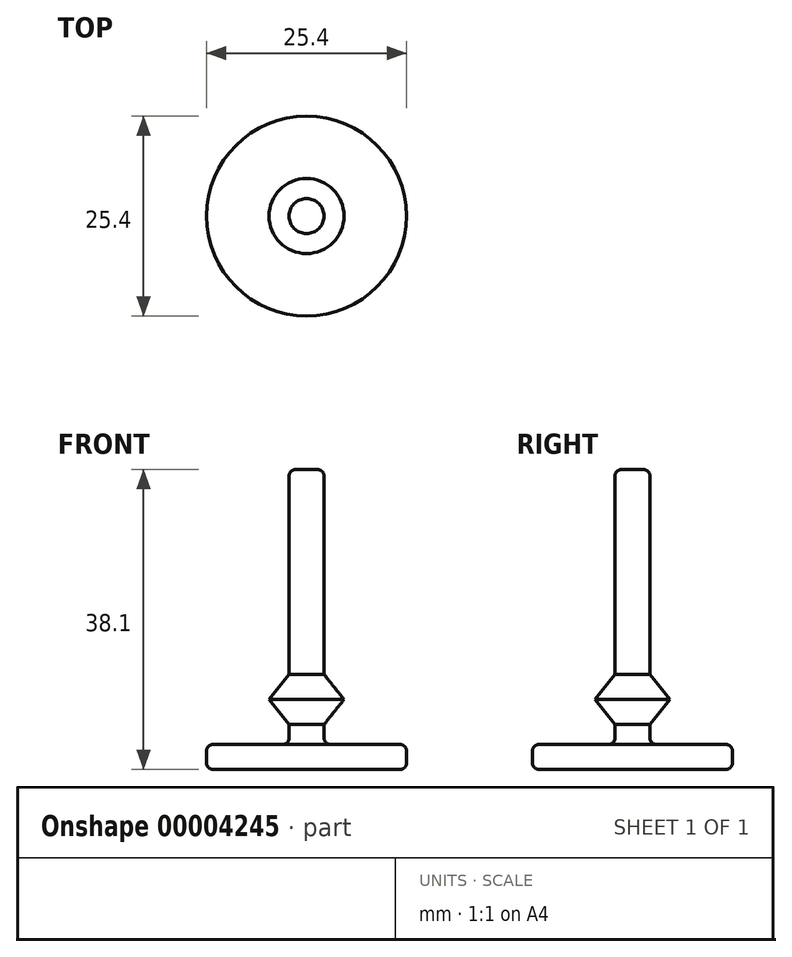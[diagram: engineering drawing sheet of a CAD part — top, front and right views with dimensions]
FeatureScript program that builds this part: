
annotation { "Feature Type Name" : "Feature", "Feature Type Description" : "" }
export const myFeature = defineFeature(function(context is Context, id is Id, definition is map)
    precondition{}
    {
        {
            var Q0;
            Q0=qCreatedBy(makeId("Front.planeOp"),FACE);
            var sketch = newSketch(context, id + "F0", { "sketchPlane" : qUnion([Q0])});
            skLineSegment(sketch, "E0", {"start": v(0, 0) * mm, "end": v(-11.87, 0) * mm});
            skLineSegment(sketch, "E1", {"start": v(-12.7, 0.83) * mm, "end": v(-12.7, 2.35) * mm});
            skLineSegment(sketch, "E2", {"start": v(-11.87, 3.18) * mm, "end": v(-3.05, 3.18) * mm});
            skLineSegment(sketch, "E3", {"start": v(-2.22, 15.23) * mm, "end": v(-2.22, 38.1) * mm});
            skLineSegment(sketch, "E4", {"start": v(-1.4, 38.1) * mm, "end": v(0, 38.1) * mm});
            skLineSegment(sketch, "E5", {"start": v(0, 38.1) * mm, "end": v(0, 0) * mm});
            skLineSegment(sketch, "E6", {"start": v(-2.22, 37.27) * mm, "end": v(-2.22, 12.07) * mm});
            skLineSegment(sketch, "E7", {"start": v(-2.22, 5.72) * mm, "end": v(-4.76, 8.9) * mm});
            skLineSegment(sketch, "E8", {"start": v(-4.76, 8.9) * mm, "end": v(-2.22, 12.07) * mm});
            skLineSegment(sketch, "E9.trimOffspring", {"start": v(-2.22, 5.72) * mm, "end": v(-2.22, 4) * mm});
            skPoint(sketch, "E10.visualSharp", {"position": v(-2.22, 3.18) * mm});
            skArc(sketch, "E10.filletArc", {"start": v(-3.05, 3.18) * mm, "mid": v(-2.47, 3.42) * mm, "end": v(-2.22, 4) * mm});
            skPoint(sketch, "E11.visualSharp", {"position": v(-12.7, 3.18) * mm});
            skArc(sketch, "E11.filletArc", {"start": v(-11.87, 3.18) * mm, "mid": v(-12.46, 2.93) * mm, "end": v(-12.7, 2.35) * mm});
            skPoint(sketch, "E12.visualSharp", {"position": v(-12.7, 0) * mm});
            skArc(sketch, "E12.filletArc", {"start": v(-12.7, 0.83) * mm, "mid": v(-12.46, 0.24) * mm, "end": v(-11.87, 0) * mm});
            skPoint(sketch, "E13.visualSharp", {"position": v(-2.22, 38.1) * mm});
            skArc(sketch, "E13.filletArc", {"start": v(-1.4, 38.1) * mm, "mid": v(-1.98, 37.86) * mm, "end": v(-2.22, 37.27) * mm});
            skSolve(sketch);
        }
        {
            var Q0;
            Q0=makeQuery(id+"F0.imprint","IMPRINT",FACE,{"disambiguationData":[TD([[makeQuery(id+"F0.imprint","IMPRINT",EDGE,{"derivedFrom":sQuery(id+"F0.wireOp",EDGE,"E0")}),-1.0]])]});
            var Q1;
            Q1=sQuery(id+"F0.wireOp",EDGE,"E5");
            revolve(context, id + "F1", {"entities" : qUnion([Q0]), "axis" : qUnion([Q1]), "revolveType" : RevolveType.FULL});
        }
    });
